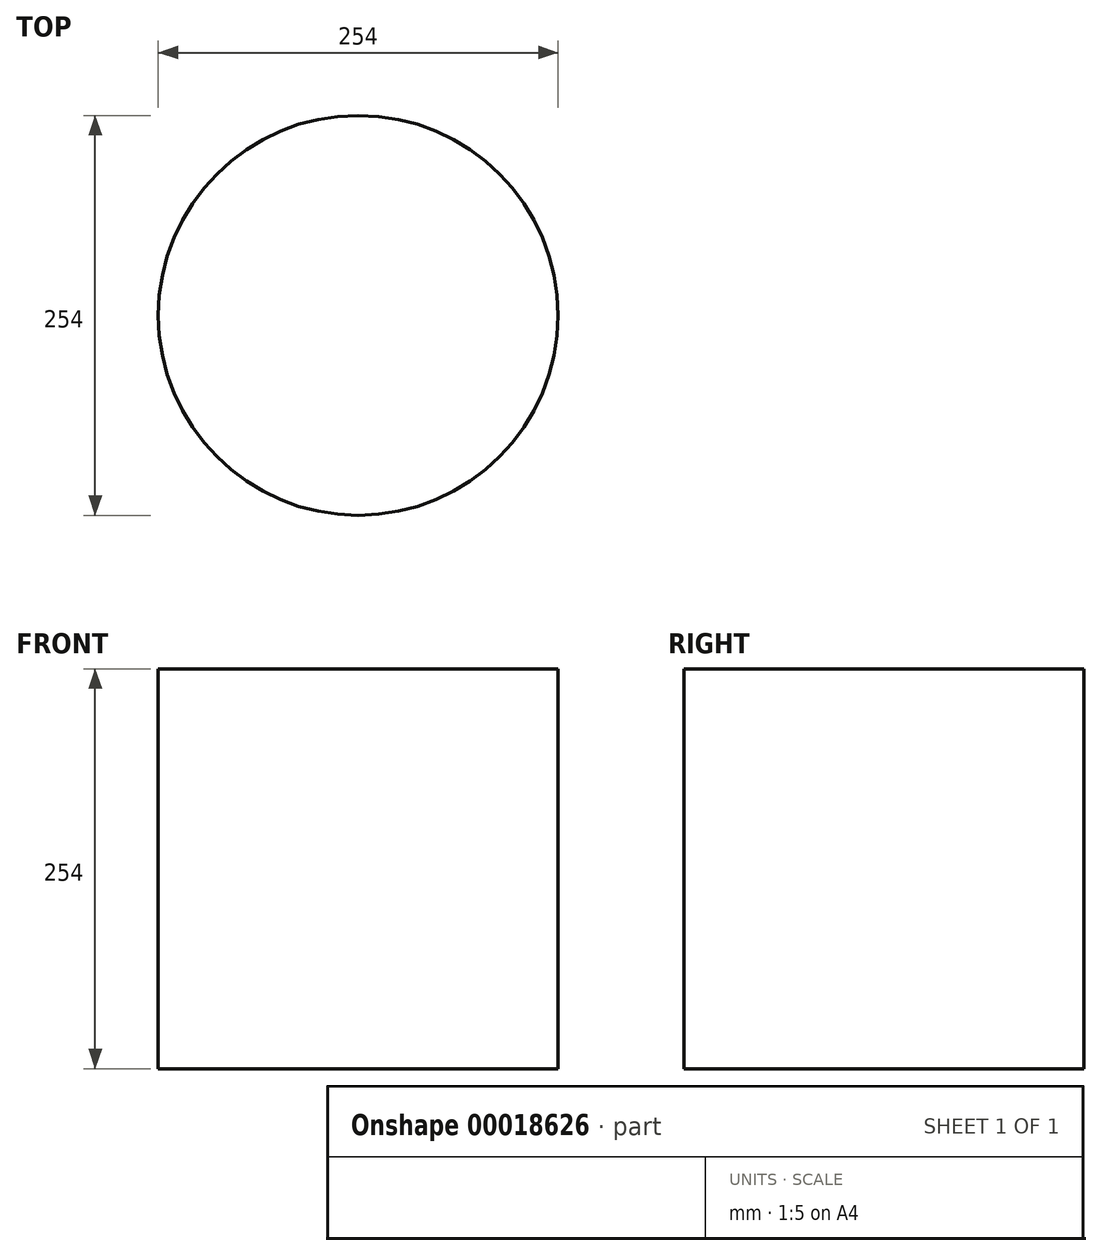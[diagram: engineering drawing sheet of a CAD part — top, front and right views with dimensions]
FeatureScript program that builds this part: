
annotation { "Feature Type Name" : "Feature", "Feature Type Description" : "" }
export const myFeature = defineFeature(function(context is Context, id is Id, definition is map)
    precondition{}
    {
        {
            var Q0;
            Q0=qCreatedBy(makeId("Top.planeOp"),FACE);
            var sketch = newSketch(context, id + "F0", { "sketchPlane" : qUnion([Q0])});
            skCircle(sketch, "E0", {"center": v(-45.48, 10.12) * mm, "radius": 127 * mm});
            skSolve(sketch);
        }
        {
            var Q0;
            Q0=makeQuery(id+"F0.imprint","IMPRINT",FACE,{"disambiguationData":[TD([[makeQuery(id+"F0.imprint","IMPRINT",EDGE,{"derivedFrom":sQuery(id+"F0.wireOp",EDGE,"E0")}),1.0]])]});
            extrude(context, id + "F1", {"entities" : qUnion([Q0]), "depth" : 254 * mm});
        }
    });
